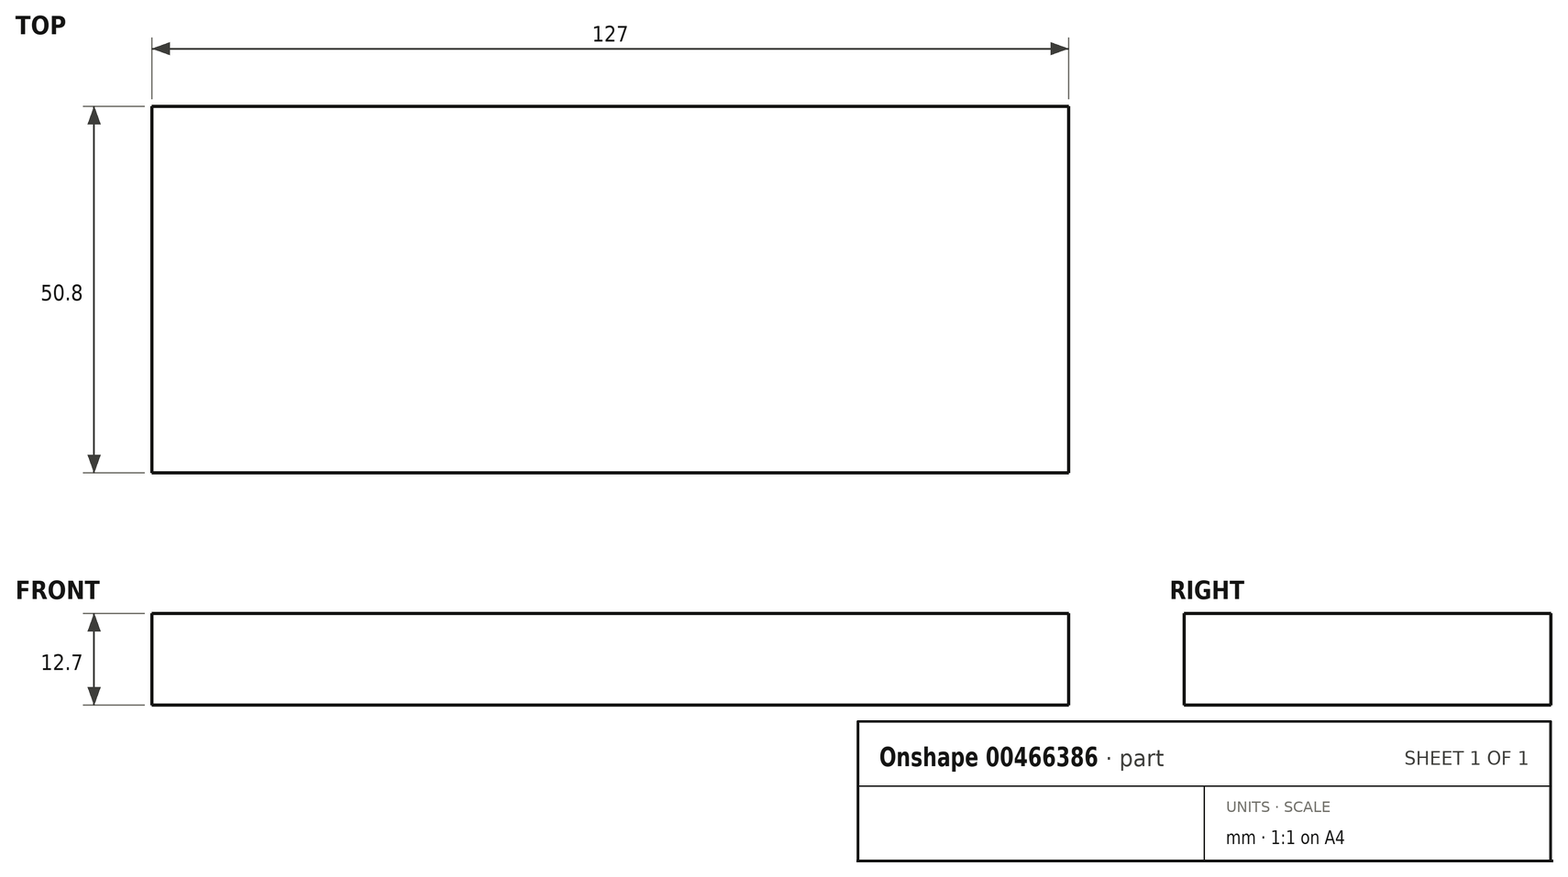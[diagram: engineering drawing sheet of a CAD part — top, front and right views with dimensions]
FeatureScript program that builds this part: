
annotation { "Feature Type Name" : "Feature", "Feature Type Description" : "" }
export const myFeature = defineFeature(function(context is Context, id is Id, definition is map)
    precondition{}
    {
        {
            var Q0;
            Q0=qCreatedBy(makeId("Top.planeOp"),FACE);
            var sketch = newSketch(context, id + "F0", { "sketchPlane" : qUnion([Q0])});
            skLineSegment(sketch, "E0.bottom", {"start": v(63.5, -25.4) * mm, "end": v(-63.5, -25.4) * mm});
            skLineSegment(sketch, "E0.top", {"start": v(63.5, 25.4) * mm, "end": v(-63.5, 25.4) * mm});
            skLineSegment(sketch, "E0.left", {"start": v(63.5, -25.4) * mm, "end": v(63.5, 25.4) * mm});
            skLineSegment(sketch, "E0.right", {"start": v(-63.5, -25.4) * mm, "end": v(-63.5, 25.4) * mm});
            skPoint(sketch, "E0.middle", {"position": v(0, 0) * mm});
            skSolve(sketch);
        }
        {
            var Q0;
            Q0 = qSketchRegion(id + "F0", true);
            extrude(context, id + "F1", {"entities" : qUnion([Q0]), "depth" : 12.7 * mm, "offsetDistance" : 25.4 * mm});
        }
    });
